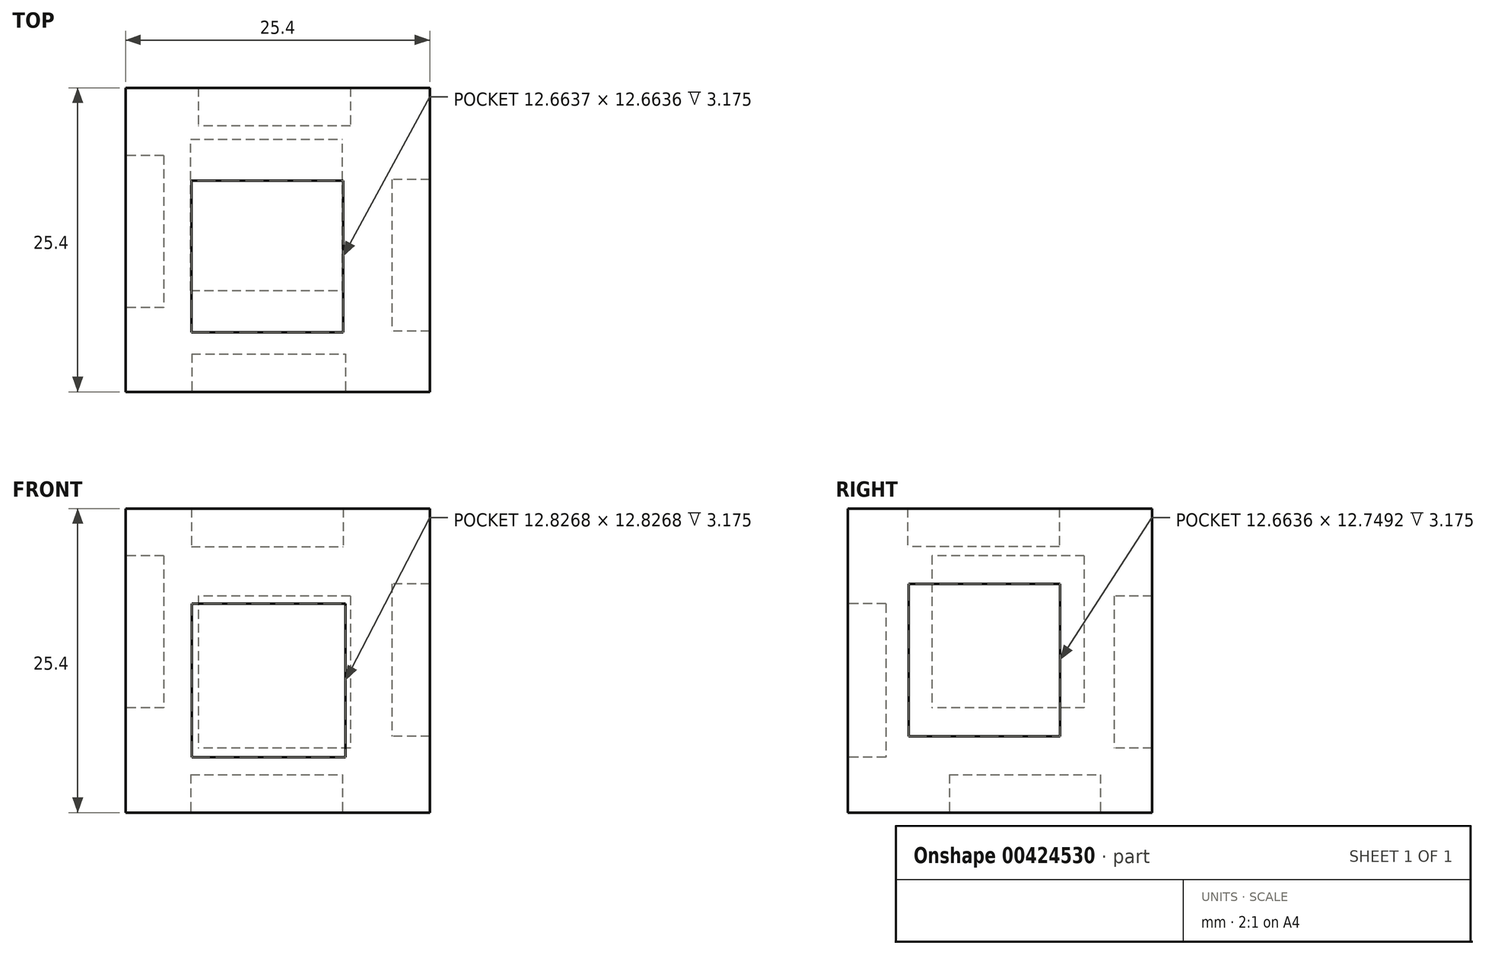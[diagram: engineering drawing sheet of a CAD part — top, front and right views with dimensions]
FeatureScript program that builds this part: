
annotation { "Feature Type Name" : "Feature", "Feature Type Description" : "" }
export const myFeature = defineFeature(function(context is Context, id is Id, definition is map)
    precondition{}
    {
        {
            var Q0;
            Q0=qCreatedBy(makeId("Front.planeOp"),FACE);
            var sketch = newSketch(context, id + "F0", { "sketchPlane" : qUnion([Q0])});
            skLineSegment(sketch, "E0.bottom", {"start": v(-49.85, 25.4) * mm, "end": v(-24.45, 25.4) * mm});
            skLineSegment(sketch, "E0.top", {"start": v(-49.85, 0) * mm, "end": v(-24.45, 0) * mm});
            skLineSegment(sketch, "E0.left", {"start": v(-49.85, 25.4) * mm, "end": v(-49.85, 0) * mm});
            skLineSegment(sketch, "E0.right", {"start": v(-24.45, 25.4) * mm, "end": v(-24.45, 0) * mm});
            skSolve(sketch);
        }
        {
            var Q0;
            Q0=makeQuery(id+"F0.imprint","IMPRINT",FACE,{"disambiguationData":[TD([[makeQuery(id+"F0.imprint","IMPRINT",EDGE,{"derivedFrom":sQuery(id+"F0.wireOp",EDGE,"E0.bottom")}),-1.0]])]});
            extrude(context, id + "F1", {"entities" : qUnion([Q0]), "depth" : 25.4 * mm});
        }
        {
            var Q0;
            Q0=makeQuery(id+"F1.opExtrude","CAP_FACE",FACE,{"disambiguationData":[OSD([sQuery(id+"F0.wireOp",EDGE,"E0.bottom"),sQuery(id+"F0.wireOp",EDGE,"E0.top"),sQuery(id+"F0.wireOp",EDGE,"E0.left"),sQuery(id+"F0.wireOp",EDGE,"E0.right")])],"isStart":false});
            var sketch = newSketch(context, id + "F2", { "sketchPlane" : qUnion([Q0])});
            skLineSegment(sketch, "E1.bottom", {"start": v(-43.05, 18.34) * mm, "end": v(-30.35, 18.34) * mm});
            skLineSegment(sketch, "E1.top", {"start": v(-43.05, 5.64) * mm, "end": v(-30.35, 5.64) * mm});
            skLineSegment(sketch, "E1.left", {"start": v(-43.05, 18.34) * mm, "end": v(-43.05, 5.64) * mm});
            skLineSegment(sketch, "E1.right", {"start": v(-30.35, 18.34) * mm, "end": v(-30.35, 5.64) * mm});
            skSolve(sketch);
        }
        {
            var Q0;
            Q0=makeQuery(id+"F2.imprint","IMPRINT",FACE,{"disambiguationData":[TD([[makeQuery(id+"F2.imprint","IMPRINT",EDGE,{"derivedFrom":sQuery(id+"F2.wireOp",EDGE,"E1.bottom")}),-1.0]])]});
            extrude(context, id + "F3", {"entities" : qUnion([Q0]), "operationType" : NewBodyOperationType.REMOVE, "oppositeDirection" : true, "depth" : 3.17 * mm});
        }
        {
            var Q0;
            Q0=makeQuery(id+"F1.opExtrude","SWEPT_FACE",FACE,{"disambiguationData":[OSD([sQuery(id+"F0.wireOp",EDGE,"E0.left")])]});
            var sketch = newSketch(context, id + "F4", { "sketchPlane" : qUnion([Q0])});
            skLineSegment(sketch, "E2.bottom", {"start": v(5.67, 21.46) * mm, "end": v(18.37, 21.46) * mm});
            skLineSegment(sketch, "E2.top", {"start": v(5.67, 8.76) * mm, "end": v(18.37, 8.76) * mm});
            skLineSegment(sketch, "E2.left", {"start": v(5.67, 21.46) * mm, "end": v(5.67, 8.76) * mm});
            skLineSegment(sketch, "E2.right", {"start": v(18.37, 21.46) * mm, "end": v(18.37, 8.76) * mm});
            skSolve(sketch);
        }
        {
            var Q0;
            Q0=makeQuery(id+"F4.imprint","IMPRINT",FACE,{"disambiguationData":[TD([[makeQuery(id+"F4.imprint","IMPRINT",EDGE,{"derivedFrom":sQuery(id+"F4.wireOp",EDGE,"E2.bottom")}),-1.0]])]});
            extrude(context, id + "F5", {"entities" : qUnion([Q0]), "operationType" : NewBodyOperationType.REMOVE, "oppositeDirection" : true, "depth" : 3.17 * mm});
        }
        {
            var Q0;
            Q0=makeQuery(id+"F1.opExtrude","CAP_FACE",FACE,{"disambiguationData":[OSD([sQuery(id+"F0.wireOp",EDGE,"E0.bottom"),sQuery(id+"F0.wireOp",EDGE,"E0.top"),sQuery(id+"F0.wireOp",EDGE,"E0.left"),sQuery(id+"F0.wireOp",EDGE,"E0.right")])],"isStart":true});
            var sketch = newSketch(context, id + "F6", { "sketchPlane" : qUnion([Q0])});
            skLineSegment(sketch, "E3.bottom", {"start": v(31.08, 18.08) * mm, "end": v(43.78, 18.08) * mm});
            skLineSegment(sketch, "E3.top", {"start": v(31.08, 5.38) * mm, "end": v(43.78, 5.38) * mm});
            skLineSegment(sketch, "E3.left", {"start": v(31.08, 18.08) * mm, "end": v(31.08, 5.38) * mm});
            skLineSegment(sketch, "E3.right", {"start": v(43.78, 18.08) * mm, "end": v(43.78, 5.38) * mm});
            skSolve(sketch);
        }
        {
            var Q0;
            Q0=makeQuery(id+"F6.imprint","IMPRINT",FACE,{"disambiguationData":[TD([[makeQuery(id+"F6.imprint","IMPRINT",EDGE,{"derivedFrom":sQuery(id+"F6.wireOp",EDGE,"E3.bottom")}),-1.0]])]});
            extrude(context, id + "F7", {"entities" : qUnion([Q0]), "operationType" : NewBodyOperationType.REMOVE, "oppositeDirection" : true, "depth" : 3.17 * mm});
        }
        {
            var Q0;
            Q0=makeQuery(id+"F7.boolean.opBoolean","COPY",FACE,{"derivedFrom":makeQuery(id+"F7.opExtrude","CAP_FACE",FACE,{"disambiguationData":[OSD([sQuery(id+"F6.wireOp",EDGE,"E3.bottom"),sQuery(id+"F6.wireOp",EDGE,"E3.top"),sQuery(id+"F6.wireOp",EDGE,"E3.left"),sQuery(id+"F6.wireOp",EDGE,"E3.right")])],"isStart":false})});
            var sketch = newSketch(context, id + "F8", { "sketchPlane" : qUnion([Q0])});
            skLineSegment(sketch, "E4.bottom", {"start": v(31.08, 18.08) * mm, "end": v(43.78, 18.08) * mm});
            skLineSegment(sketch, "E4.top", {"start": v(31.08, 5.38) * mm, "end": v(43.78, 5.38) * mm});
            skLineSegment(sketch, "E4.left", {"start": v(31.08, 18.08) * mm, "end": v(31.08, 5.38) * mm});
            skLineSegment(sketch, "E4.right", {"start": v(43.78, 18.08) * mm, "end": v(43.78, 5.38) * mm});
            skSolve(sketch);
        }
        {
            var Q0;
            Q0=makeQuery(id+"F8.imprint","IMPRINT",FACE,{"disambiguationData":[TD([[makeQuery(id+"F8.imprint","IMPRINT",EDGE,{"derivedFrom":sQuery(id+"F8.wireOp",EDGE,"E4.bottom")}),-1.0]])]});
            extrude(context, id + "F9", {"entities" : qUnion([Q0]), "depth" : 3.17 * mm});
        }
        {
            var Q0;
            Q0=makeQuery(id+"F3.boolean.opBoolean","COPY",FACE,{"derivedFrom":makeQuery(id+"F3.opExtrude","CAP_FACE",FACE,{"disambiguationData":[OSD([sQuery(id+"F2.wireOp",EDGE,"E1.bottom"),sQuery(id+"F2.wireOp",EDGE,"E1.top"),sQuery(id+"F2.wireOp",EDGE,"E1.left"),sQuery(id+"F2.wireOp",EDGE,"E1.right")])],"isStart":false})});
            var sketch = newSketch(context, id + "F10", { "sketchPlane" : qUnion([Q0])});
            skLineSegment(sketch, "E5.bottom", {"start": v(-43.05, 18.34) * mm, "end": v(-30.35, 18.34) * mm});
            skLineSegment(sketch, "E5.top", {"start": v(-43.05, 5.64) * mm, "end": v(-30.35, 5.64) * mm});
            skLineSegment(sketch, "E5.left", {"start": v(-43.05, 18.34) * mm, "end": v(-43.05, 5.64) * mm});
            skLineSegment(sketch, "E5.right", {"start": v(-30.35, 18.34) * mm, "end": v(-30.35, 5.64) * mm});
            skSolve(sketch);
        }
        {
            var Q0;
            Q0=makeQuery(id+"F10.imprint","IMPRINT",FACE,{"disambiguationData":[TD([[makeQuery(id+"F10.imprint","IMPRINT",EDGE,{"derivedFrom":sQuery(id+"F10.wireOp",EDGE,"E5.bottom")}),-1.0]])]});
            extrude(context, id + "F11", {"entities" : qUnion([Q0]), "operationType" : NewBodyOperationType.ADD, "depth" : 3.17 * mm});
        }
        {
            var Q0;
            Q0=makeQuery(id+"F1.opExtrude","SWEPT_FACE",FACE,{"disambiguationData":[OSD([sQuery(id+"F0.wireOp",EDGE,"E0.left")])]});
            var sketch = newSketch(context, id + "F12", { "sketchPlane" : qUnion([Q0])});
            skLineSegment(sketch, "E6.bottom", {"start": v(5.67, 21.46) * mm, "end": v(18.37, 21.46) * mm});
            skLineSegment(sketch, "E6.top", {"start": v(5.67, 8.76) * mm, "end": v(18.37, 8.76) * mm});
            skLineSegment(sketch, "E6.left", {"start": v(5.67, 21.46) * mm, "end": v(5.67, 8.76) * mm});
            skLineSegment(sketch, "E6.right", {"start": v(18.37, 21.46) * mm, "end": v(18.37, 8.76) * mm});
            skSolve(sketch);
        }
        {
            var Q0;
            Q0=makeQuery(id+"F12.imprint","IMPRINT",FACE,{"disambiguationData":[TD([[makeQuery(id+"F12.imprint","IMPRINT",EDGE,{"derivedFrom":sQuery(id+"F12.wireOp",EDGE,"E6.bottom")}),-1.0]])]});
            extrude(context, id + "F13", {"entities" : qUnion([Q0]), "depth" : 3.17 * mm});
        }
        {
            var Q0;
            Q0=makeQuery(id+"F13.opExtrude","SWEPT_BODY",BODY,{"disambiguationData":[OSD([sQuery(id+"F12.wireOp",EDGE,"E6.bottom"),sQuery(id+"F12.wireOp",EDGE,"E6.top"),sQuery(id+"F12.wireOp",EDGE,"E6.left"),sQuery(id+"F12.wireOp",EDGE,"E6.right")])]});
            deleteBodies(context, id + "F14", {"entities" : qUnion([Q0])});
        }
        {
            var Q0;
            Q0=makeQuery(id+"F5.boolean.opBoolean","COPY",FACE,{"derivedFrom":makeQuery(id+"F5.opExtrude","CAP_FACE",FACE,{"disambiguationData":[OSD([sQuery(id+"F4.wireOp",EDGE,"E2.bottom"),sQuery(id+"F4.wireOp",EDGE,"E2.top"),sQuery(id+"F4.wireOp",EDGE,"E2.left"),sQuery(id+"F4.wireOp",EDGE,"E2.right")])],"isStart":false})});
            var sketch = newSketch(context, id + "F15", { "sketchPlane" : qUnion([Q0])});
            skLineSegment(sketch, "E7.bottom", {"start": v(5.67, 21.46) * mm, "end": v(18.37, 21.46) * mm});
            skLineSegment(sketch, "E7.top", {"start": v(5.67, 8.76) * mm, "end": v(18.37, 8.76) * mm});
            skLineSegment(sketch, "E7.left", {"start": v(5.67, 21.46) * mm, "end": v(5.67, 8.76) * mm});
            skLineSegment(sketch, "E7.right", {"start": v(18.37, 21.46) * mm, "end": v(18.37, 8.76) * mm});
            skSolve(sketch);
        }
        {
            var Q0;
            Q0 = qSketchRegion(id + "F15", true);
            extrude(context, id + "F16", {"entities" : qUnion([Q0]), "depth" : 3.17 * mm});
        }
        {
            var Q0;
            Q0=makeQuery(id+"F1.opExtrude","SWEPT_FACE",FACE,{"disambiguationData":[OSD([sQuery(id+"F0.wireOp",EDGE,"E0.top")])]});
            var sketch = newSketch(context, id + "F17", { "sketchPlane" : qUnion([Q0])});
            skLineSegment(sketch, "E8.bottom", {"start": v(-43.6, 17.75) * mm, "end": v(-30.93, 17.75) * mm});
            skLineSegment(sketch, "E8.top", {"start": v(-43.6, 5.01) * mm, "end": v(-30.93, 5.01) * mm});
            skLineSegment(sketch, "E8.left", {"start": v(-43.6, 17.75) * mm, "end": v(-43.6, 5.01) * mm});
            skLineSegment(sketch, "E8.right", {"start": v(-30.93, 17.75) * mm, "end": v(-30.93, 5.01) * mm});
            skSolve(sketch);
        }
        {
            var Q0;
            Q0=makeQuery(id+"F17.imprint","IMPRINT",FACE,{"disambiguationData":[TD([[makeQuery(id+"F17.imprint","IMPRINT",EDGE,{"derivedFrom":sQuery(id+"F17.wireOp",EDGE,"E8.bottom")}),-1.0]])]});
            extrude(context, id + "F18", {"entities" : qUnion([Q0]), "operationType" : NewBodyOperationType.REMOVE, "oppositeDirection" : true, "depth" : 3.17 * mm});
        }
        {
            var Q0;
            Q0=makeQuery(id+"F18.boolean.opBoolean","COPY",FACE,{"derivedFrom":makeQuery(id+"F18.opExtrude","CAP_FACE",FACE,{"disambiguationData":[OSD([sQuery(id+"F17.wireOp",EDGE,"E8.bottom"),sQuery(id+"F17.wireOp",EDGE,"E8.top"),sQuery(id+"F17.wireOp",EDGE,"E8.left"),sQuery(id+"F17.wireOp",EDGE,"E8.right")])],"isStart":false})});
            extrude(context, id + "F19", {"entities" : qUnion([Q0]), "operationType" : NewBodyOperationType.ADD, "depth" : 3.17 * mm});
        }
        {
            var Q0;
            Q0=makeQuery(id+"F19.boolean.opBoolean","MERGE",FACE,{"derivedFrom":[makeQuery(id+"F1.opExtrude","SWEPT_FACE",FACE,{"disambiguationData":[OSD([sQuery(id+"F0.wireOp",EDGE,"E0.top")])]}),makeQuery(id+"F19.opExtrude","CAP_FACE",FACE,{"disambiguationData":[OSD([sQuery(id+"F17.wireOp",EDGE,"E8.bottom"),sQuery(id+"F17.wireOp",EDGE,"E8.top"),sQuery(id+"F17.wireOp",EDGE,"E8.left"),sQuery(id+"F17.wireOp",EDGE,"E8.right")])],"isStart":false})]});
            var sketch = newSketch(context, id + "F20", { "sketchPlane" : qUnion([Q0])});
            skLineSegment(sketch, "E9.bottom", {"start": v(-44.42, 16.93) * mm, "end": v(-31.75, 16.93) * mm});
            skLineSegment(sketch, "E9.top", {"start": v(-44.42, 4.31) * mm, "end": v(-31.75, 4.31) * mm});
            skLineSegment(sketch, "E9.left", {"start": v(-44.42, 16.93) * mm, "end": v(-44.42, 4.31) * mm});
            skLineSegment(sketch, "E9.right", {"start": v(-31.75, 16.93) * mm, "end": v(-31.75, 4.31) * mm});
            skSolve(sketch);
        }
        {
            var Q0;
            Q0=makeQuery(id+"F20.imprint","IMPRINT",FACE,{"disambiguationData":[TD([[makeQuery(id+"F20.imprint","IMPRINT",EDGE,{"derivedFrom":sQuery(id+"F20.wireOp",EDGE,"E9.bottom")}),-1.0]])]});
            extrude(context, id + "F21", {"entities" : qUnion([Q0]), "operationType" : NewBodyOperationType.REMOVE, "oppositeDirection" : true, "depth" : 3.17 * mm});
        }
        {
            var Q0;
            Q0=makeQuery(id+"F21.boolean.opBoolean","COPY",FACE,{"derivedFrom":makeQuery(id+"F21.opExtrude","CAP_FACE",FACE,{"disambiguationData":[OSD([sQuery(id+"F20.wireOp",EDGE,"E9.bottom"),sQuery(id+"F20.wireOp",EDGE,"E9.top"),sQuery(id+"F20.wireOp",EDGE,"E9.left"),sQuery(id+"F20.wireOp",EDGE,"E9.right")])],"isStart":false})});
            var sketch = newSketch(context, id + "F22", { "sketchPlane" : qUnion([Q0])});
            skLineSegment(sketch, "E10.bottom", {"start": v(-44.42, 16.93) * mm, "end": v(-31.75, 16.93) * mm});
            skLineSegment(sketch, "E10.top", {"start": v(-44.42, 4.31) * mm, "end": v(-31.75, 4.31) * mm});
            skLineSegment(sketch, "E10.left", {"start": v(-44.42, 16.93) * mm, "end": v(-44.42, 4.31) * mm});
            skLineSegment(sketch, "E10.right", {"start": v(-31.75, 16.93) * mm, "end": v(-31.75, 4.31) * mm});
            skSolve(sketch);
        }
        {
            var Q0;
            Q0 = qSketchRegion(id + "F22", true);
            extrude(context, id + "F23", {"entities" : qUnion([Q0]), "depth" : 3.17 * mm});
        }
        {
            var Q0;
            Q0=makeQuery(id+"F1.opExtrude","SWEPT_FACE",FACE,{"disambiguationData":[OSD([sQuery(id+"F0.wireOp",EDGE,"E0.bottom")])]});
            var sketch = newSketch(context, id + "F24", { "sketchPlane" : qUnion([Q0])});
            skLineSegment(sketch, "E11.bottom", {"start": v(-44.36, -7.76) * mm, "end": v(-31.7, -7.76) * mm});
            skLineSegment(sketch, "E11.top", {"start": v(-44.36, -20.42) * mm, "end": v(-31.7, -20.42) * mm});
            skLineSegment(sketch, "E11.left", {"start": v(-44.36, -7.76) * mm, "end": v(-44.36, -20.42) * mm});
            skLineSegment(sketch, "E11.right", {"start": v(-31.7, -7.76) * mm, "end": v(-31.7, -20.42) * mm});
            skSolve(sketch);
        }
        {
            var Q0;
            Q0 = qSketchRegion(id + "F24", true);
            extrude(context, id + "F25", {"entities" : qUnion([Q0]), "operationType" : NewBodyOperationType.REMOVE, "oppositeDirection" : true, "depth" : 3.17 * mm});
        }
        {
            var Q0;
            Q0=makeQuery(id+"F1.opExtrude","SWEPT_FACE",FACE,{"disambiguationData":[OSD([sQuery(id+"F0.wireOp",EDGE,"E0.right")])]});
            var sketch = newSketch(context, id + "F26", { "sketchPlane" : qUnion([Q0])});
            skLineSegment(sketch, "E12.bottom", {"start": v(-7.67, 19.11) * mm, "end": v(-20.34, 19.11) * mm});
            skLineSegment(sketch, "E12.top", {"start": v(-7.67, 6.37) * mm, "end": v(-20.34, 6.37) * mm});
            skLineSegment(sketch, "E12.left", {"start": v(-7.67, 19.11) * mm, "end": v(-7.67, 6.37) * mm});
            skLineSegment(sketch, "E12.right", {"start": v(-20.34, 19.11) * mm, "end": v(-20.34, 6.37) * mm});
            skSolve(sketch);
        }
        {
            var Q0;
            Q0=makeQuery(id+"F26.imprint","IMPRINT",FACE,{"disambiguationData":[TD([[makeQuery(id+"F26.imprint","IMPRINT",EDGE,{"derivedFrom":sQuery(id+"F26.wireOp",EDGE,"E12.bottom")}),1.0]])]});
            extrude(context, id + "F27", {"entities" : qUnion([Q0]), "operationType" : NewBodyOperationType.REMOVE, "oppositeDirection" : true, "depth" : 3.17 * mm});
        }
        {
            var Q0;
            Q0=makeQuery(id+"F11.boolean.opBoolean","MERGE",FACE,{"derivedFrom":[makeQuery(id+"F1.opExtrude","CAP_FACE",FACE,{"disambiguationData":[OSD([sQuery(id+"F0.wireOp",EDGE,"E0.bottom"),sQuery(id+"F0.wireOp",EDGE,"E0.top"),sQuery(id+"F0.wireOp",EDGE,"E0.left"),sQuery(id+"F0.wireOp",EDGE,"E0.right")])],"isStart":false}),makeQuery(id+"F11.opExtrude","CAP_FACE",FACE,{"disambiguationData":[OSD([sQuery(id+"F10.wireOp",EDGE,"E5.bottom"),sQuery(id+"F10.wireOp",EDGE,"E5.top"),sQuery(id+"F10.wireOp",EDGE,"E5.left"),sQuery(id+"F10.wireOp",EDGE,"E5.right")])],"isStart":false})]});
            var sketch = newSketch(context, id + "F28", { "sketchPlane" : qUnion([Q0])});
            skLineSegment(sketch, "E13.bottom", {"start": v(-44.33, 17.44) * mm, "end": v(-31.5, 17.44) * mm});
            skLineSegment(sketch, "E13.top", {"start": v(-44.33, 4.61) * mm, "end": v(-31.5, 4.61) * mm});
            skLineSegment(sketch, "E13.left", {"start": v(-44.33, 17.44) * mm, "end": v(-44.33, 4.61) * mm});
            skLineSegment(sketch, "E13.right", {"start": v(-31.5, 17.44) * mm, "end": v(-31.5, 4.61) * mm});
            skSolve(sketch);
        }
        {
            var Q0;
            Q0 = qSketchRegion(id + "F28", true);
            extrude(context, id + "F29", {"entities" : qUnion([Q0]), "operationType" : NewBodyOperationType.REMOVE, "oppositeDirection" : true, "depth" : 3.17 * mm});
        }
        {
            var Q0;
            Q0=makeQuery(id+"F27.boolean.opBoolean","COPY",FACE,{"derivedFrom":makeQuery(id+"F27.opExtrude","CAP_FACE",FACE,{"disambiguationData":[OSD([sQuery(id+"F26.wireOp",EDGE,"E12.bottom"),sQuery(id+"F26.wireOp",EDGE,"E12.top"),sQuery(id+"F26.wireOp",EDGE,"E12.left"),sQuery(id+"F26.wireOp",EDGE,"E12.right")])],"isStart":false})});
            var sketch = newSketch(context, id + "F30", { "sketchPlane" : qUnion([Q0])});
            skLineSegment(sketch, "E14.bottom", {"start": v(-7.67, 6.37) * mm, "end": v(-20.34, 6.37) * mm});
            skLineSegment(sketch, "E14.top", {"start": v(-7.67, 19.11) * mm, "end": v(-20.34, 19.11) * mm});
            skLineSegment(sketch, "E14.left", {"start": v(-7.67, 6.37) * mm, "end": v(-7.67, 19.11) * mm});
            skLineSegment(sketch, "E14.right", {"start": v(-20.34, 6.37) * mm, "end": v(-20.34, 19.11) * mm});
            skSolve(sketch);
        }
        {
            var Q0;
            Q0=makeQuery(id+"F30.imprint","IMPRINT",FACE,{"disambiguationData":[TD([[makeQuery(id+"F30.imprint","IMPRINT",EDGE,{"derivedFrom":sQuery(id+"F30.wireOp",EDGE,"E14.bottom")}),-1.0]])]});
            extrude(context, id + "F31", {"entities" : qUnion([Q0]), "depth" : 3.17 * mm});
        }
        {
            var Q0;
            Q0=makeQuery(id+"F29.boolean.opBoolean","COPY",FACE,{"derivedFrom":makeQuery(id+"F29.opExtrude","CAP_FACE",FACE,{"disambiguationData":[OSD([sQuery(id+"F28.wireOp",EDGE,"E13.bottom"),sQuery(id+"F28.wireOp",EDGE,"E13.top"),sQuery(id+"F28.wireOp",EDGE,"E13.left"),sQuery(id+"F28.wireOp",EDGE,"E13.right")])],"isStart":false})});
            var sketch = newSketch(context, id + "F32", { "sketchPlane" : qUnion([Q0])});
            skLineSegment(sketch, "E15.bottom", {"start": v(-44.33, 17.44) * mm, "end": v(-31.5, 17.44) * mm});
            skLineSegment(sketch, "E15.top", {"start": v(-44.33, 4.61) * mm, "end": v(-31.5, 4.61) * mm});
            skLineSegment(sketch, "E15.left", {"start": v(-44.33, 17.44) * mm, "end": v(-44.33, 4.61) * mm});
            skLineSegment(sketch, "E15.right", {"start": v(-31.5, 17.44) * mm, "end": v(-31.5, 4.61) * mm});
            skSolve(sketch);
        }
        {
            var Q0;
            Q0 = qSketchRegion(id + "F32", true);
            extrude(context, id + "F33", {"entities" : qUnion([Q0]), "depth" : 3.17 * mm});
        }
        {
            var Q0;
            Q0=makeQuery(id+"F25.boolean.opBoolean","COPY",FACE,{"derivedFrom":makeQuery(id+"F25.opExtrude","CAP_FACE",FACE,{"disambiguationData":[OSD([sQuery(id+"F24.wireOp",EDGE,"E11.bottom"),sQuery(id+"F24.wireOp",EDGE,"E11.top"),sQuery(id+"F24.wireOp",EDGE,"E11.left"),sQuery(id+"F24.wireOp",EDGE,"E11.right")])],"isStart":false})});
            var sketch = newSketch(context, id + "F34", { "sketchPlane" : qUnion([Q0])});
            skLineSegment(sketch, "E16.bottom", {"start": v(-44.36, -7.76) * mm, "end": v(-31.7, -7.76) * mm});
            skLineSegment(sketch, "E16.top", {"start": v(-44.36, -20.42) * mm, "end": v(-31.7, -20.42) * mm});
            skLineSegment(sketch, "E16.left", {"start": v(-44.36, -7.76) * mm, "end": v(-44.36, -20.42) * mm});
            skLineSegment(sketch, "E16.right", {"start": v(-31.7, -7.76) * mm, "end": v(-31.7, -20.42) * mm});
            skSolve(sketch);
        }
        {
            var Q0;
            Q0 = qSketchRegion(id + "F34", true);
            extrude(context, id + "F35", {"entities" : qUnion([Q0]), "depth" : 3.17 * mm});
        }
    });
